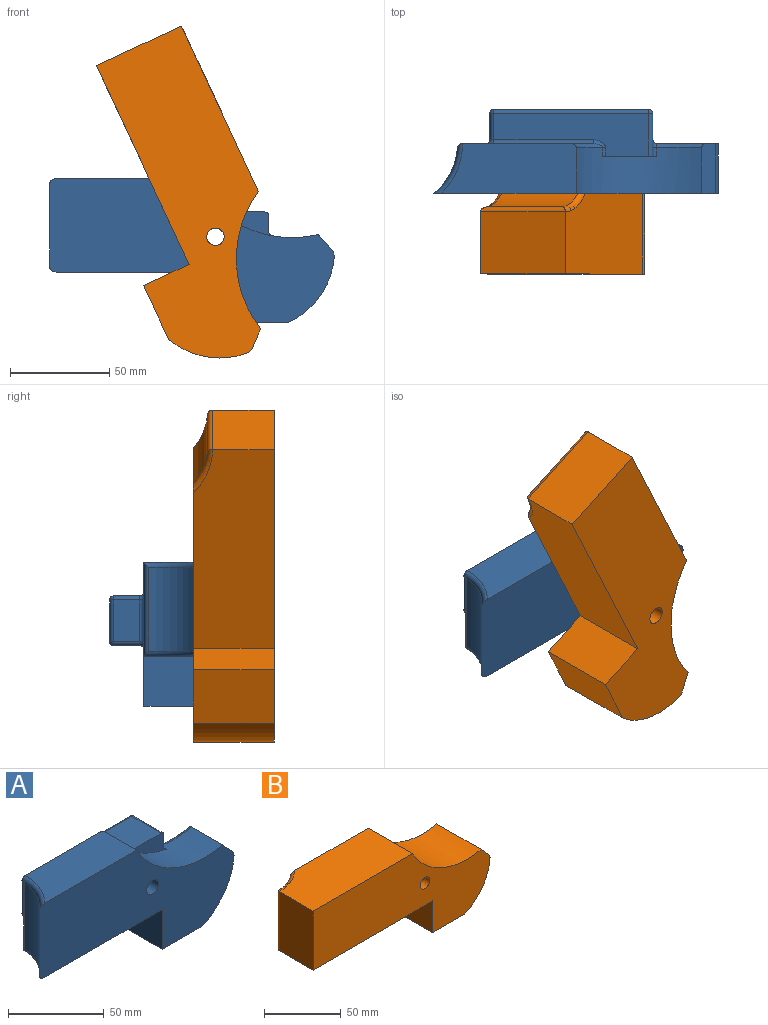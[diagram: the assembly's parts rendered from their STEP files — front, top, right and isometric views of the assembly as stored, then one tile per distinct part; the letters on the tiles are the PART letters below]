
ASSEMBLY  parts=2 mates=1
PART A: 48 faces, bbox 143.5x48x73.6 mm
  f0: cylinder r=57.44mm len=63.41mm, axis (0,1,0), area 1586.6mm2, adj f1,f10,f16,f22,f23,f27,f28,f47
  f1: plane 67.95x25mm, normal (0,0,1), area 1513.3mm2, adj f0,f7,f12,f23,f47
  f2: cylinder r=40mm len=32.78mm, axis (0,1,0), area 1049.8mm2, adj f5,f11,f12,f47
  f3: plane 86.7x25mm, normal (0,0,-1), area 1983mm2, adj f4,f8,f12,f47
  f4: plane 25.37x25mm, normal (-1,0,0), area 634.2mm2, adj f3,f5,f12,f47
  f5: plane 29.83x25mm, normal (0,0,-1), area 745.7mm2, adj f2,f4,f12,f47
  f6: cylinder r=32.05mm len=42.19mm, axis (0,0,1), area 1110.5mm2, adj f7,f8,f13,f47
  f7: torus R=34.59mm, axis (0,0,1), area 109.9mm2, adj f1,f6,f12,f13,f47
  f8: torus R=34.59mm, axis (0,0,1), area 109.9mm2, adj f3,f6,f12,f13,f47
  f9: cylinder r=4.4mm len=40.29mm, axis (0,1,0), area 1113.8mm2, adj f45,f47
  f10: plane 25x7.71mm, normal (0.74,0,0.67), area 258.9mm2, adj f0,f11,f12,f27,f47
  f11: cylinder r=5mm len=25mm, axis (0,1,0), area 103mm2, adj f2,f10,f12,f47
  f12: plane 129.04x72.64mm, normal (0,1,0), area 3163.5mm2, adj f1,f2,f3,f4,f5,f7,f8,f10
  f13: cylinder r=2.54mm len=47.27mm, axis (0,0,1), area 172.7mm2, adj f6,f7,f8,f12
  f14: plane 21x13.29mm, normal (-1,0,0), area 279.1mm2, adj f31,f32,f40,f41
  f15: plane 78.23x13.29mm, normal (0,0,-1), area 1039.6mm2, adj f30,f39,f40,f44
  f16: plane 26.87x12.52mm, normal (0,-1,0), area 174.5mm2, adj f0,f17,f18,f20,f22,f28
  f17: plane 21.6x21mm, normal (1,0,0), area 349.8mm2, adj f16,f20,f28,f29,f34,f38,f39
  f18: plane 78.23x21.6mm, normal (0,0,1), area 1227.1mm2, adj f16,f20,f21,f22,f26,f32,f33
  f19: plane 78.23x21mm, normal (0,1,0), area 1483.2mm2, adj f21,f29,f30,f31,f46
  f20: cylinder r=2mm len=21.6mm, axis (0,1,0), area 67.9mm2, adj f16,f17,f18,f24
  f21: cylinder r=2mm len=78.23mm, axis (-1,0,0), area 245.8mm2, adj f18,f19,f24,f25
  f22: cylinder r=2mm len=4.31mm, axis (0,1,0), area 6mm2, adj f0,f16,f18,f26
  f23: torus R=59.44mm, axis (0,-1,0), area 64mm2, adj f0,f1,f12,f26
  f24: sphere r=2mm, area 6.3mm2, adj f20,f21,f29
  f25: sphere r=2mm, area 6.3mm2, adj f21,f31,f32
  f26: bspline ~6.33x4.4mm, area 14.2mm2, adj f18,f22,f23,f33
  f27: torus R=59.44mm, axis (0,-1,0), area 74.3mm2, adj f0,f10,f12,f34
  f28: cylinder r=2mm len=4.31mm, axis (0,1,0), area 12mm2, adj f0,f16,f17,f34
  f29: cylinder r=2mm len=21mm, axis (0,0,1), area 66mm2, adj f17,f19,f24,f35
  f30: cylinder r=2mm len=78.23mm, axis (1,0,0), area 245.8mm2, adj f15,f19,f35,f36
  f31: cylinder r=2mm len=21mm, axis (0,0,-1), area 66mm2, adj f14,f19,f25,f36
  f32: cylinder r=2mm len=13.29mm, axis (0,-1,0), area 41.8mm2, adj f14,f18,f25,f37
  f33: cylinder r=2mm len=50.34mm, axis (-1,0,0), area 158.1mm2, adj f12,f18,f26,f37
  f34: bspline ~4.88x4.72mm, area 12.9mm2, adj f17,f27,f28,f38
  f35: sphere r=2mm, area 6.3mm2, adj f29,f30,f39
  f36: sphere r=2mm, area 6.3mm2, adj f30,f31,f40
  f37: torus R=4mm, axis (0,-1,0), area 13.5mm2, adj f12,f32,f33,f41
  f38: cylinder r=2mm len=8.85mm, axis (0,0,1), area 27.8mm2, adj f12,f17,f34,f42
  f39: cylinder r=2mm len=13.29mm, axis (0,-1,0), area 41.8mm2, adj f15,f17,f35,f42
  f40: cylinder r=2mm len=13.29mm, axis (0,1,0), area 41.8mm2, adj f14,f15,f36,f43
  f41: cylinder r=2mm len=21mm, axis (0,0,-1), area 66mm2, adj f12,f14,f37,f43
  f42: torus R=4mm, axis (0,-1,0), area 13.5mm2, adj f12,f38,f39,f44
  f43: torus R=4mm, axis (0,-1,0), area 13.5mm2, adj f12,f40,f41,f44
  f44: cylinder r=2mm len=78.23mm, axis (1,0,0), area 245.8mm2, adj f12,f15,f42,f43
  f45: plane 14.25x14.25mm, normal (0,1,0), area 98.7mm2, adj f9,f46
  f46: cylinder r=7.12mm len=14.25mm, axis (0,1,0), area 89.5mm2, adj f19,f45
  f47: plane 143.48x72.64mm, normal (0,-1,0), area 6102mm2, adj f0,f1,f2,f3,f4,f5,f6,f7
PART B: 16 faces, bbox 163.5x42.6x72.6 mm
  f0: cylinder r=2.54mm len=47.27mm, axis (0,0,1), area 172.7mm2, adj f1,f6,f7,f8
  f1: plane 47.27x31.29mm, normal (-1,0,0), area 1479.1mm2, adj f0,f3,f6,f7,f9,f13
  f2: cylinder r=4.4mm len=40.79mm, axis (0,1,0), area 1127.6mm2, adj f3,f15
  f3: plane 163.54x72.64mm, normal (0,-1,0), area 7054.3mm2, adj f1,f2,f4,f5,f9,f10,f11,f12
  f4: plane 40.79x29.83mm, normal (0,0,-1), area 1216.6mm2, adj f3,f5,f12,f15
  f5: plane 40.79x25.37mm, normal (-1,0,0), area 1034.7mm2, adj f3,f4,f9,f15
  f6: torus R=34.59mm, axis (0,0,1), area 90mm2, adj f0,f1,f8,f9,f15
  f7: torus R=34.59mm, axis (0,0,1), area 90mm2, adj f0,f1,f8,f13,f15
  f8: cylinder r=32.05mm len=42.19mm, axis (0,0,1), area 814.9mm2, adj f0,f6,f7,f15
  f9: plane 110.6x40.79mm, normal (0,0,-1), area 4353.3mm2, adj f1,f3,f5,f6,f15
  f10: cylinder r=5mm len=40.79mm, axis (0,1,0), area 168.1mm2, adj f3,f11,f12,f15
  f11: plane 40.79x7.71mm, normal (0.74,0,0.67), area 424mm2, adj f3,f10,f14,f15
  f12: cylinder r=40mm len=40.79mm, axis (0,1,0), area 1712.7mm2, adj f3,f4,f10,f15
  f13: plane 91.85x40.79mm, normal (0,0,1), area 3588.6mm2, adj f1,f3,f7,f14,f15
  f14: cylinder r=57.44mm len=63.41mm, axis (0,1,0), area 3042.7mm2, adj f3,f11,f13,f15
  f15: plane 143.48x72.64mm, normal (0,1,0), area 6102mm2, adj f2,f4,f5,f6,f7,f8,f9,f10
PLACE A t=(-28.17,0,6.27)mm
PLACE B rot(axis=(0,1,0),65deg) t=(-36.57,0,-6.31)mm
MATE revolute B.f2 <-> A.f9  axis (0,1,0) through (-42.24,-25,6.57)mm
